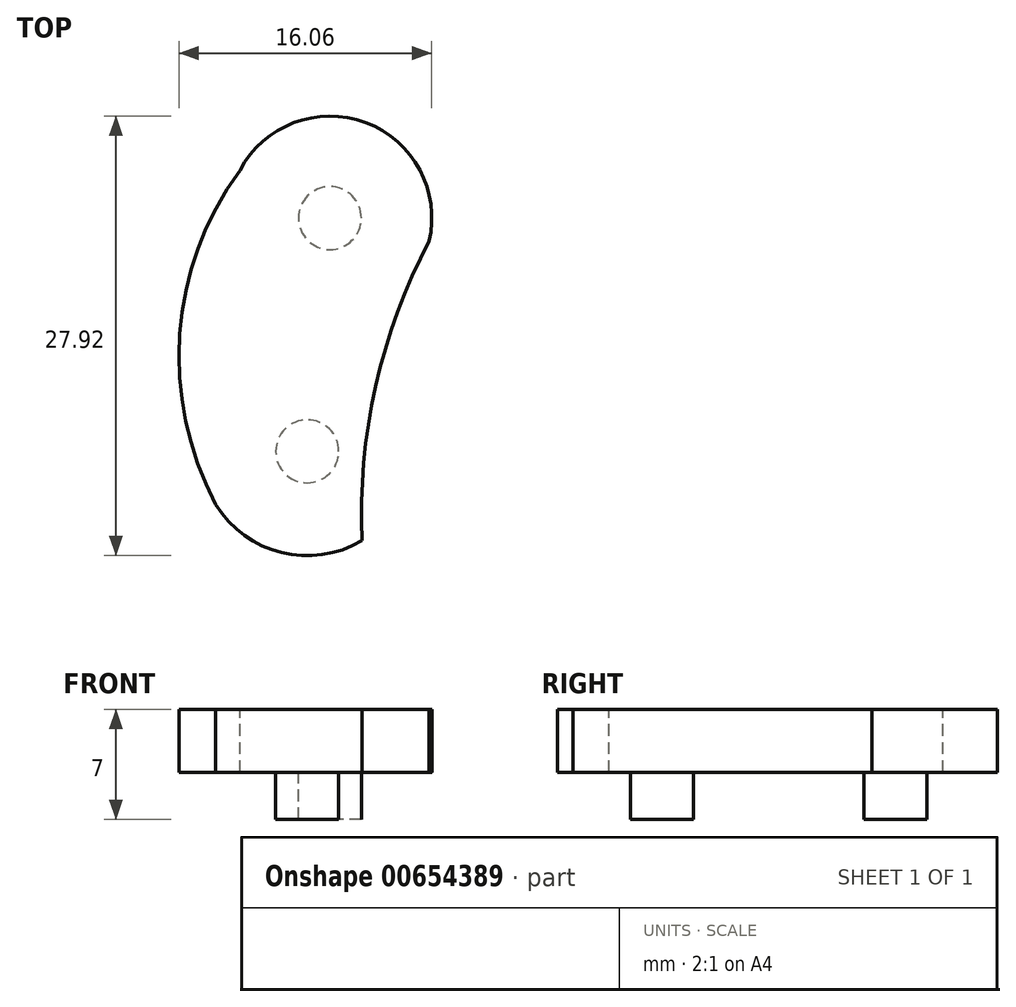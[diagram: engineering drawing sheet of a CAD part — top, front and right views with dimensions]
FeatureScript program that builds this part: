
annotation { "Feature Type Name" : "Feature", "Feature Type Description" : "" }
export const myFeature = defineFeature(function(context is Context, id is Id, definition is map)
    precondition{}
    {
        {
            var Q0;
            Q0=qCreatedBy(makeId("Top.planeOp"),FACE);
            var sketch = newSketch(context, id + "F0", { "sketchPlane" : qUnion([Q0])});
            skArc(sketch, "E0", {"start": v(-3.22, 10.47) * mm, "mid": v(-7.03, 0.09) * mm, "end": v(-4.75, -10.74) * mm});
            skArc(sketch, "E1", {"start": v(8.8, 5.97) * mm, "mid": v(4.77, 13.5) * mm, "end": v(-3.22, 10.47) * mm});
            skArc(sketch, "E2", {"start": v(-4.75, -10.74) * mm, "mid": v(-0.58, -13.8) * mm, "end": v(4.54, -13.04) * mm});
            skArc(sketch, "E3", {"start": v(8.8, 5.97) * mm, "mid": v(5.4, -3.25) * mm, "end": v(4.54, -13.04) * mm});
            skCircle(sketch, "E4", {"center": v(2.5, 7.45) * mm, "radius": 2 * mm});
            skCircle(sketch, "E5", {"center": v(1.06, -7.37) * mm, "radius": 2 * mm});
            skSolve(sketch);
        }
        {
            var Q0;
            Q0=makeQuery(id+"F0.imprint","IMPRINT",FACE,{"disambiguationData":[TD([[makeQuery(id+"F0.imprint","IMPRINT",EDGE,{"derivedFrom":sQuery(id+"F0.wireOp",EDGE,"AcFCBj5Z-fYGj-4Be1-qkaU-F5Nqu2Phsbyp")}),-1.0]])]});
            var Q1;
            Q1=makeQuery(id+"F0.imprint","IMPRINT",FACE,{"disambiguationData":[TD([[makeQuery(id+"F0.imprint","IMPRINT",EDGE,{"derivedFrom":sQuery(id+"F0.wireOp",EDGE,"E0")}),1.0]])]});
            extrude(context, id + "F1", {"entities" : qUnion([Q0, Q1]), "oppositeDirection" : true, "depth" : 4 * mm, "offsetDistance" : 25 * mm});
        }
        {
            var Q0;
            Q0=makeQuery(id+"F0.imprint","IMPRINT",FACE,{"disambiguationData":[TD([[makeQuery(id+"F0.imprint","IMPRINT",EDGE,{"derivedFrom":sQuery(id+"F0.wireOp",EDGE,"E4")}),1.0]])]});
            var Q1;
            Q1=makeQuery(id+"F0.imprint","IMPRINT",FACE,{"disambiguationData":[TD([[makeQuery(id+"F0.imprint","IMPRINT",EDGE,{"derivedFrom":sQuery(id+"F0.wireOp",EDGE,"E5")}),1.0]])]});
            extrude(context, id + "F2", {"entities" : qUnion([Q0, Q1]), "operationType" : NewBodyOperationType.ADD, "oppositeDirection" : true, "depth" : 7 * mm, "offsetDistance" : 25 * mm});
        }
    });
